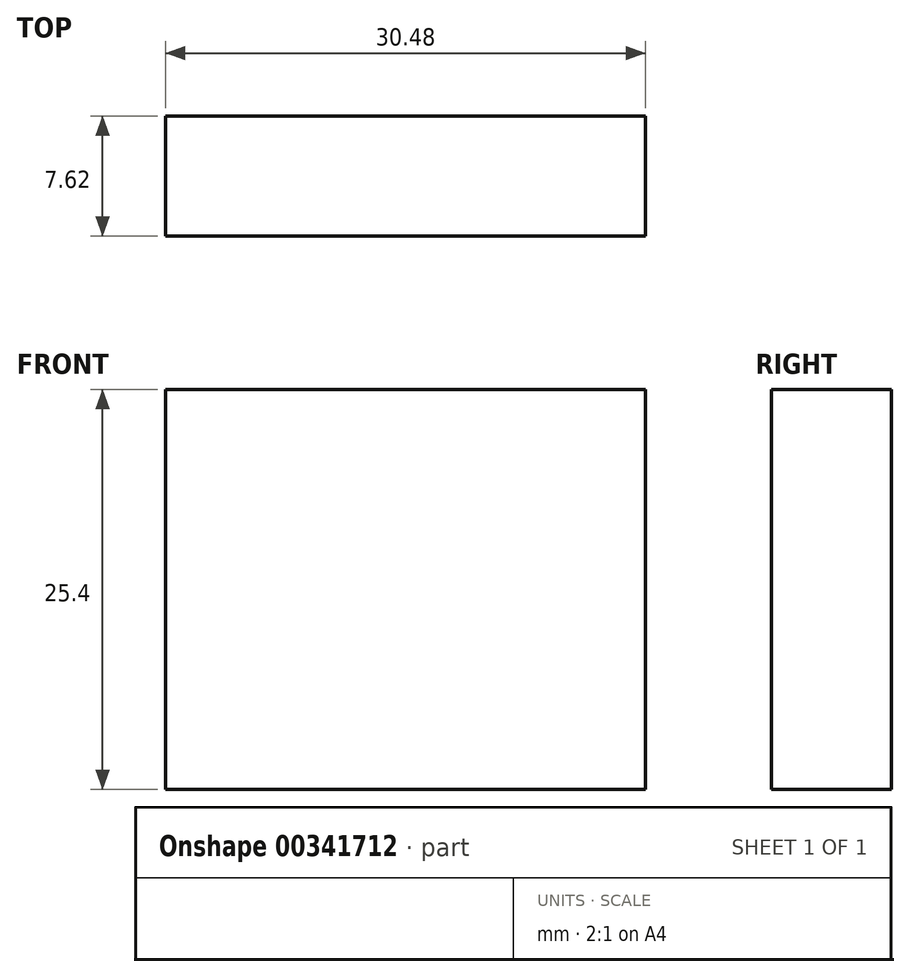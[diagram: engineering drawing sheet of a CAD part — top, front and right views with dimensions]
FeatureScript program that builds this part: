
annotation { "Feature Type Name" : "Feature", "Feature Type Description" : "" }
export const myFeature = defineFeature(function(context is Context, id is Id, definition is map)
    precondition{}
    {
        {
            var Q0;
            Q0=qCreatedBy(makeId("Top.planeOp"),FACE);
            var sketch = newSketch(context, id + "F0", { "sketchPlane" : qUnion([Q0])});
            skLineSegment(sketch, "E0", {"start": v(0, 0) * mm, "end": v(-30.48, 0) * mm});
            skLineSegment(sketch, "E1", {"start": v(-30.48, 0) * mm, "end": v(-30.48, 7.62) * mm});
            skLineSegment(sketch, "E2", {"start": v(-30.48, 7.62) * mm, "end": v(0, 7.62) * mm});
            skLineSegment(sketch, "E3", {"start": v(0, 7.62) * mm, "end": v(0, 0) * mm});
            skSolve(sketch);
        }
        {
            var Q0;
            Q0 = qSketchRegion(id + "F0", true);
            extrude(context, id + "F1", {"entities" : qUnion([Q0]), "depth" : 25.4 * mm});
        }
    });
